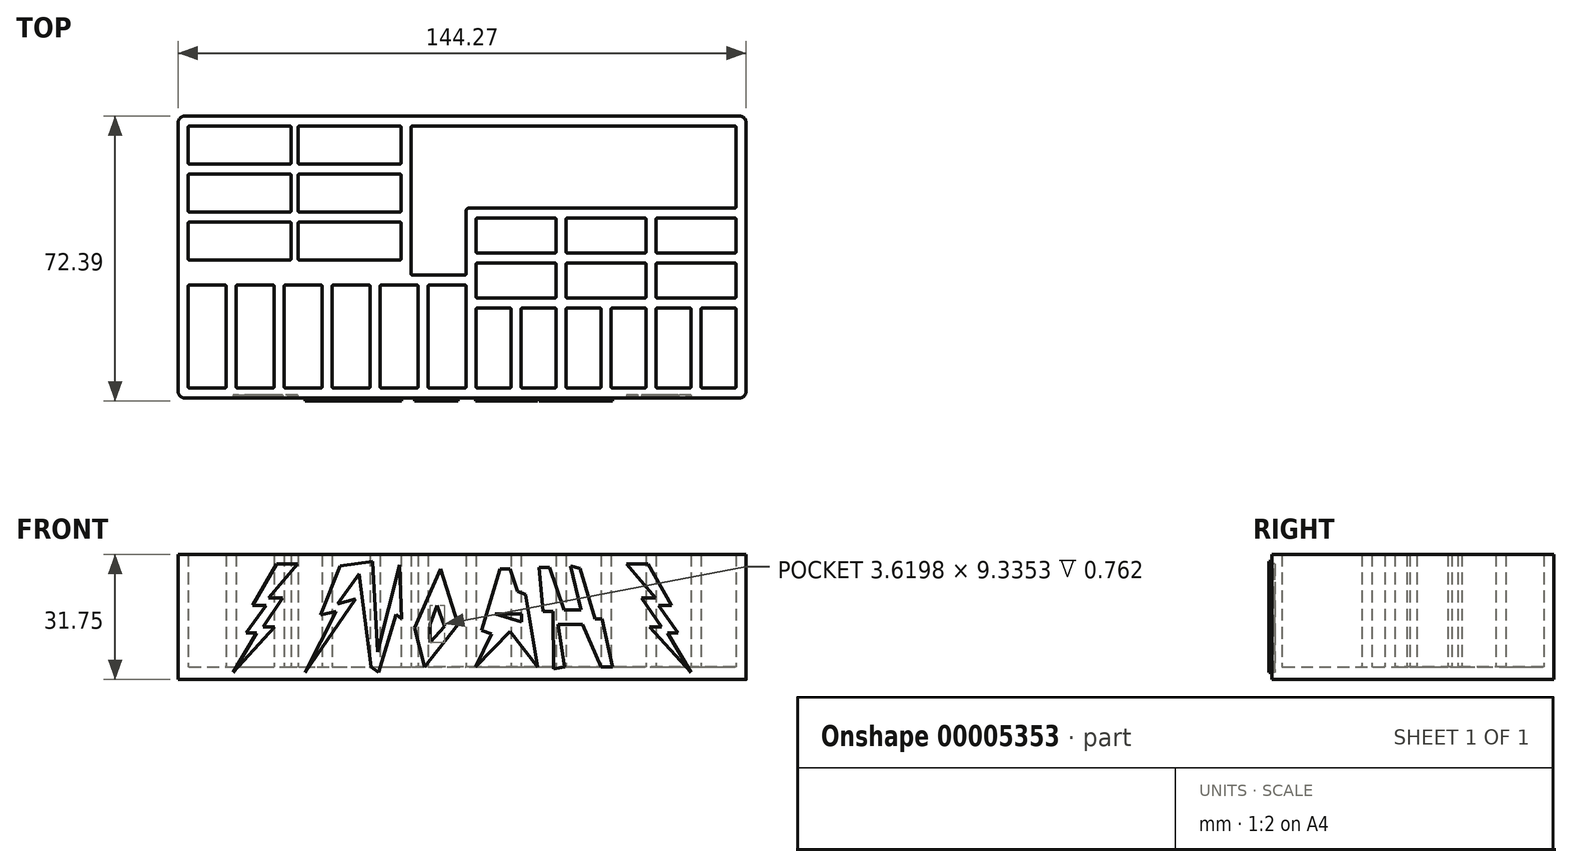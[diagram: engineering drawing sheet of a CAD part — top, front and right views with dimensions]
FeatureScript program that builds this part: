
annotation { "Feature Type Name" : "Feature", "Feature Type Description" : "" }
export const myFeature = defineFeature(function(context is Context, id is Id, definition is map)
    precondition{}
    {
        {
            var Q0;
            Q0=qCreatedBy(makeId("Top.planeOp"),FACE);
            var sketch = newSketch(context, id + "F0", { "sketchPlane" : qUnion([Q0])});
            skLineSegment(sketch, "E0.bottom", {"start": v(0.25, 0) * mm, "end": v(9.4, 0) * mm});
            skLineSegment(sketch, "E0.top", {"start": v(0.25, 26.16) * mm, "end": v(9.4, 26.16) * mm});
            skLineSegment(sketch, "E0.left", {"start": v(0, 0.25) * mm, "end": v(0, 25.9) * mm});
            skLineSegment(sketch, "E0.right", {"start": v(9.65, 0.25) * mm, "end": v(9.65, 25.9) * mm});
            skPoint(sketch, "E1.visualSharp", {"position": v(0, 26.16) * mm});
            skArc(sketch, "E1.filletArc", {"start": v(0.25, 26.16) * mm, "mid": v(0.07, 26.09) * mm, "end": v(0, 25.9) * mm});
            skPoint(sketch, "E2.visualSharp", {"position": v(9.65, 26.16) * mm});
            skArc(sketch, "E2.filletArc", {"start": v(9.65, 25.9) * mm, "mid": v(9.58, 26.09) * mm, "end": v(9.4, 26.16) * mm});
            skPoint(sketch, "E3.visualSharp", {"position": v(9.65, 0) * mm});
            skArc(sketch, "E3.filletArc", {"start": v(9.4, 0) * mm, "mid": v(9.58, 0.07) * mm, "end": v(9.65, 0.25) * mm});
            skPoint(sketch, "E4.visualSharp", {"position": v(0, 0) * mm});
            skArc(sketch, "E4.filletArc", {"start": v(0, 0.25) * mm, "mid": v(0.07, 0.07) * mm, "end": v(0.25, 0) * mm});
            skPoint(sketch, "E5.1.0.0", {"position": v(12.2, 0) * mm});
            skPoint(sketch, "E5.1.0.1", {"position": v(12.2, 26.16) * mm});
            skPoint(sketch, "E5.1.0.2", {"position": v(21.84, 26.16) * mm});
            skLineSegment(sketch, "E5.1.0.3", {"start": v(12.45, 0) * mm, "end": v(21.59, 0) * mm});
            skArc(sketch, "E5.1.0.4", {"start": v(12.2, 0.25) * mm, "mid": v(12.27, 0.07) * mm, "end": v(12.45, 0) * mm});
            skLineSegment(sketch, "E5.1.0.5", {"start": v(12.2, 0.25) * mm, "end": v(12.2, 25.9) * mm});
            skLineSegment(sketch, "E5.1.0.6", {"start": v(12.45, 26.16) * mm, "end": v(21.59, 26.16) * mm});
            skPoint(sketch, "E5.1.0.7", {"position": v(21.84, 0) * mm});
            skArc(sketch, "E5.1.0.8", {"start": v(21.84, 25.9) * mm, "mid": v(21.77, 26.09) * mm, "end": v(21.59, 26.16) * mm});
            skArc(sketch, "E5.1.0.9", {"start": v(21.59, 0) * mm, "mid": v(21.77, 0.07) * mm, "end": v(21.84, 0.25) * mm});
            skLineSegment(sketch, "E5.1.0.10", {"start": v(21.84, 0.25) * mm, "end": v(21.84, 25.9) * mm});
            skArc(sketch, "E5.1.0.11", {"start": v(12.45, 26.16) * mm, "mid": v(12.27, 26.09) * mm, "end": v(12.2, 25.9) * mm});
            skPoint(sketch, "E5.2.0.0", {"position": v(24.38, 0) * mm});
            skPoint(sketch, "E5.2.0.1", {"position": v(24.38, 26.16) * mm});
            skPoint(sketch, "E5.2.0.2", {"position": v(34.04, 26.16) * mm});
            skLineSegment(sketch, "E5.2.0.3", {"start": v(24.64, 0) * mm, "end": v(33.78, 0) * mm});
            skArc(sketch, "E5.2.0.4", {"start": v(24.38, 0.25) * mm, "mid": v(24.46, 0.07) * mm, "end": v(24.64, 0) * mm});
            skLineSegment(sketch, "E5.2.0.5", {"start": v(24.38, 0.25) * mm, "end": v(24.38, 25.9) * mm});
            skLineSegment(sketch, "E5.2.0.6", {"start": v(24.64, 26.16) * mm, "end": v(33.78, 26.16) * mm});
            skPoint(sketch, "E5.2.0.7", {"position": v(34.04, 0) * mm});
            skArc(sketch, "E5.2.0.8", {"start": v(34.04, 25.9) * mm, "mid": v(33.96, 26.09) * mm, "end": v(33.78, 26.16) * mm});
            skArc(sketch, "E5.2.0.9", {"start": v(33.78, 0) * mm, "mid": v(33.96, 0.07) * mm, "end": v(34.04, 0.25) * mm});
            skLineSegment(sketch, "E5.2.0.10", {"start": v(34.04, 0.25) * mm, "end": v(34.04, 25.9) * mm});
            skArc(sketch, "E5.2.0.11", {"start": v(24.64, 26.16) * mm, "mid": v(24.46, 26.09) * mm, "end": v(24.38, 25.9) * mm});
            skPoint(sketch, "E5.3.0.0", {"position": v(36.58, 0) * mm});
            skPoint(sketch, "E5.3.0.1", {"position": v(36.58, 26.16) * mm});
            skPoint(sketch, "E5.3.0.2", {"position": v(46.23, 26.16) * mm});
            skLineSegment(sketch, "E5.3.0.3", {"start": v(36.83, 0) * mm, "end": v(45.97, 0) * mm});
            skArc(sketch, "E5.3.0.4", {"start": v(36.58, 0.25) * mm, "mid": v(36.65, 0.07) * mm, "end": v(36.83, 0) * mm});
            skLineSegment(sketch, "E5.3.0.5", {"start": v(36.58, 0.25) * mm, "end": v(36.58, 25.9) * mm});
            skLineSegment(sketch, "E5.3.0.6", {"start": v(36.83, 26.16) * mm, "end": v(45.97, 26.16) * mm});
            skPoint(sketch, "E5.3.0.7", {"position": v(46.23, 0) * mm});
            skArc(sketch, "E5.3.0.8", {"start": v(46.23, 25.9) * mm, "mid": v(46.15, 26.09) * mm, "end": v(45.97, 26.16) * mm});
            skArc(sketch, "E5.3.0.9", {"start": v(45.97, 0) * mm, "mid": v(46.15, 0.07) * mm, "end": v(46.23, 0.25) * mm});
            skLineSegment(sketch, "E5.3.0.10", {"start": v(46.23, 0.25) * mm, "end": v(46.23, 25.9) * mm});
            skArc(sketch, "E5.3.0.11", {"start": v(36.83, 26.16) * mm, "mid": v(36.65, 26.09) * mm, "end": v(36.58, 25.9) * mm});
            skPoint(sketch, "E5.4.0.0", {"position": v(48.77, 0) * mm});
            skPoint(sketch, "E5.4.0.1", {"position": v(48.77, 26.16) * mm});
            skPoint(sketch, "E5.4.0.2", {"position": v(58.42, 26.16) * mm});
            skLineSegment(sketch, "E5.4.0.3", {"start": v(49.02, 0) * mm, "end": v(58.17, 0) * mm});
            skArc(sketch, "E5.4.0.4", {"start": v(48.77, 0.25) * mm, "mid": v(48.84, 0.07) * mm, "end": v(49.02, 0) * mm});
            skLineSegment(sketch, "E5.4.0.5", {"start": v(48.77, 0.25) * mm, "end": v(48.77, 25.9) * mm});
            skLineSegment(sketch, "E5.4.0.6", {"start": v(49.02, 26.16) * mm, "end": v(58.17, 26.16) * mm});
            skPoint(sketch, "E5.4.0.7", {"position": v(58.42, 0) * mm});
            skArc(sketch, "E5.4.0.8", {"start": v(58.42, 25.9) * mm, "mid": v(58.35, 26.09) * mm, "end": v(58.17, 26.16) * mm});
            skArc(sketch, "E5.4.0.9", {"start": v(58.17, 0) * mm, "mid": v(58.35, 0.07) * mm, "end": v(58.42, 0.25) * mm});
            skLineSegment(sketch, "E5.4.0.10", {"start": v(58.42, 0.25) * mm, "end": v(58.42, 25.9) * mm});
            skArc(sketch, "E5.4.0.11", {"start": v(49.02, 26.16) * mm, "mid": v(48.84, 26.09) * mm, "end": v(48.77, 25.9) * mm});
            skPoint(sketch, "E5.5.0.0", {"position": v(60.96, 0) * mm});
            skPoint(sketch, "E5.5.0.1", {"position": v(60.96, 26.16) * mm});
            skPoint(sketch, "E5.5.0.2", {"position": v(70.61, 26.16) * mm});
            skLineSegment(sketch, "E5.5.0.3", {"start": v(61.21, 0) * mm, "end": v(70.36, 0) * mm});
            skArc(sketch, "E5.5.0.4", {"start": v(60.96, 0.25) * mm, "mid": v(61.03, 0.07) * mm, "end": v(61.21, 0) * mm});
            skLineSegment(sketch, "E5.5.0.5", {"start": v(60.96, 0.25) * mm, "end": v(60.96, 25.9) * mm});
            skLineSegment(sketch, "E5.5.0.6", {"start": v(61.21, 26.16) * mm, "end": v(70.36, 26.16) * mm});
            skPoint(sketch, "E5.5.0.7", {"position": v(70.61, 0) * mm});
            skArc(sketch, "E5.5.0.8", {"start": v(70.61, 25.9) * mm, "mid": v(70.54, 26.09) * mm, "end": v(70.36, 26.16) * mm});
            skArc(sketch, "E5.5.0.9", {"start": v(70.36, 0) * mm, "mid": v(70.54, 0.07) * mm, "end": v(70.61, 0.25) * mm});
            skLineSegment(sketch, "E5.5.0.10", {"start": v(70.61, 0.25) * mm, "end": v(70.61, 25.9) * mm});
            skArc(sketch, "E5.5.0.11", {"start": v(61.21, 26.16) * mm, "mid": v(61.03, 26.09) * mm, "end": v(60.96, 25.9) * mm});
            skLineSegment(sketch, "E5.direction1", {"start": v(0, 0) * mm, "end": v(12.2, 0) * mm, "construction": true});
            skLineSegment(sketch, "E6.bottom", {"start": v(73.4, 0) * mm, "end": v(81.79, 0) * mm});
            skLineSegment(sketch, "E6.top", {"start": v(73.4, 20.32) * mm, "end": v(81.79, 20.32) * mm});
            skLineSegment(sketch, "E6.left", {"start": v(73.15, 0.25) * mm, "end": v(73.15, 20.07) * mm});
            skLineSegment(sketch, "E6.right", {"start": v(82.04, 0.25) * mm, "end": v(82.04, 20.07) * mm});
            skPoint(sketch, "E7.visualSharp", {"position": v(73.15, 20.32) * mm});
            skArc(sketch, "E7.filletArc", {"start": v(73.4, 20.32) * mm, "mid": v(73.23, 20.25) * mm, "end": v(73.15, 20.07) * mm});
            skPoint(sketch, "E8.visualSharp", {"position": v(82.04, 20.32) * mm});
            skArc(sketch, "E8.filletArc", {"start": v(82.04, 20.07) * mm, "mid": v(81.97, 20.25) * mm, "end": v(81.79, 20.32) * mm});
            skPoint(sketch, "E9.visualSharp", {"position": v(82.04, 0) * mm});
            skArc(sketch, "E9.filletArc", {"start": v(81.79, 0) * mm, "mid": v(81.97, 0.07) * mm, "end": v(82.04, 0.25) * mm});
            skPoint(sketch, "E10.visualSharp", {"position": v(73.15, 0) * mm});
            skArc(sketch, "E10.filletArc", {"start": v(73.15, 0.25) * mm, "mid": v(73.23, 0.07) * mm, "end": v(73.4, 0) * mm});
            skLineSegment(sketch, "E11.bottom", {"start": v(0.25, 32.51) * mm, "end": v(25.9, 32.51) * mm});
            skLineSegment(sketch, "E11.top", {"start": v(0.25, 42.16) * mm, "end": v(25.9, 42.16) * mm});
            skLineSegment(sketch, "E11.left", {"start": v(0, 32.77) * mm, "end": v(0, 41.91) * mm});
            skLineSegment(sketch, "E11.right", {"start": v(26.16, 32.77) * mm, "end": v(26.16, 41.91) * mm});
            skPoint(sketch, "E12.visualSharp", {"position": v(0, 42.16) * mm});
            skArc(sketch, "E12.filletArc", {"start": v(0.25, 42.16) * mm, "mid": v(0.07, 42.09) * mm, "end": v(0, 41.91) * mm});
            skPoint(sketch, "E13.visualSharp", {"position": v(26.16, 42.16) * mm});
            skArc(sketch, "E13.filletArc", {"start": v(26.16, 41.91) * mm, "mid": v(26.09, 42.09) * mm, "end": v(25.9, 42.16) * mm});
            skPoint(sketch, "E14.visualSharp", {"position": v(26.16, 32.51) * mm});
            skArc(sketch, "E14.filletArc", {"start": v(25.9, 32.51) * mm, "mid": v(26.09, 32.59) * mm, "end": v(26.16, 32.77) * mm});
            skPoint(sketch, "E15.visualSharp", {"position": v(0, 32.51) * mm});
            skArc(sketch, "E15.filletArc", {"start": v(0, 32.77) * mm, "mid": v(0.07, 32.59) * mm, "end": v(0.25, 32.51) * mm});
            skLineSegment(sketch, "E16.0.1.0", {"start": v(0, 44.96) * mm, "end": v(0, 54.1) * mm});
            skPoint(sketch, "E16.0.1.1", {"position": v(0, 54.36) * mm});
            skArc(sketch, "E16.0.1.2", {"start": v(0.25, 54.36) * mm, "mid": v(0.07, 54.28) * mm, "end": v(0, 54.1) * mm});
            skLineSegment(sketch, "E16.0.1.3", {"start": v(0.25, 54.36) * mm, "end": v(25.9, 54.36) * mm});
            skPoint(sketch, "E16.0.1.4", {"position": v(26.16, 44.7) * mm});
            skPoint(sketch, "E16.0.1.5", {"position": v(26.16, 54.36) * mm});
            skLineSegment(sketch, "E16.0.1.6", {"start": v(0.25, 44.7) * mm, "end": v(25.9, 44.7) * mm});
            skPoint(sketch, "E16.0.1.7", {"position": v(0, 44.7) * mm});
            skLineSegment(sketch, "E16.0.1.8", {"start": v(26.16, 44.96) * mm, "end": v(26.16, 54.1) * mm});
            skArc(sketch, "E16.0.1.9", {"start": v(26.16, 54.1) * mm, "mid": v(26.09, 54.28) * mm, "end": v(25.9, 54.36) * mm});
            skArc(sketch, "E16.0.1.10", {"start": v(25.9, 44.7) * mm, "mid": v(26.09, 44.78) * mm, "end": v(26.16, 44.96) * mm});
            skArc(sketch, "E16.0.1.11", {"start": v(0, 44.96) * mm, "mid": v(0.07, 44.78) * mm, "end": v(0.25, 44.7) * mm});
            skLineSegment(sketch, "E16.1.0.0", {"start": v(27.94, 32.77) * mm, "end": v(27.94, 41.91) * mm});
            skPoint(sketch, "E16.1.0.1", {"position": v(27.94, 42.16) * mm});
            skArc(sketch, "E16.1.0.2", {"start": v(28.2, 42.16) * mm, "mid": v(28.01, 42.09) * mm, "end": v(27.94, 41.91) * mm});
            skLineSegment(sketch, "E16.1.0.3", {"start": v(28.2, 42.16) * mm, "end": v(53.85, 42.16) * mm});
            skPoint(sketch, "E16.1.0.4", {"position": v(54.1, 32.51) * mm});
            skPoint(sketch, "E16.1.0.5", {"position": v(54.1, 42.16) * mm});
            skLineSegment(sketch, "E16.1.0.6", {"start": v(28.2, 32.51) * mm, "end": v(53.85, 32.51) * mm});
            skPoint(sketch, "E16.1.0.7", {"position": v(27.94, 32.51) * mm});
            skLineSegment(sketch, "E16.1.0.8", {"start": v(54.1, 32.77) * mm, "end": v(54.1, 41.91) * mm});
            skArc(sketch, "E16.1.0.9", {"start": v(54.1, 41.91) * mm, "mid": v(54.03, 42.09) * mm, "end": v(53.85, 42.16) * mm});
            skArc(sketch, "E16.1.0.10", {"start": v(53.85, 32.51) * mm, "mid": v(54.03, 32.59) * mm, "end": v(54.1, 32.77) * mm});
            skArc(sketch, "E16.1.0.11", {"start": v(27.94, 32.77) * mm, "mid": v(28.01, 32.59) * mm, "end": v(28.2, 32.51) * mm});
            skLineSegment(sketch, "E16.1.1.0", {"start": v(27.94, 44.96) * mm, "end": v(27.94, 54.1) * mm});
            skPoint(sketch, "E16.1.1.1", {"position": v(27.94, 54.36) * mm});
            skArc(sketch, "E16.1.1.2", {"start": v(28.2, 54.36) * mm, "mid": v(28.01, 54.28) * mm, "end": v(27.94, 54.1) * mm});
            skLineSegment(sketch, "E16.1.1.3", {"start": v(28.2, 54.36) * mm, "end": v(53.85, 54.36) * mm});
            skPoint(sketch, "E16.1.1.4", {"position": v(54.1, 44.7) * mm});
            skPoint(sketch, "E16.1.1.5", {"position": v(54.1, 54.36) * mm});
            skLineSegment(sketch, "E16.1.1.6", {"start": v(28.2, 44.7) * mm, "end": v(53.85, 44.7) * mm});
            skPoint(sketch, "E16.1.1.7", {"position": v(27.94, 44.7) * mm});
            skLineSegment(sketch, "E16.1.1.8", {"start": v(54.1, 44.96) * mm, "end": v(54.1, 54.1) * mm});
            skArc(sketch, "E16.1.1.9", {"start": v(54.1, 54.1) * mm, "mid": v(54.03, 54.28) * mm, "end": v(53.85, 54.36) * mm});
            skArc(sketch, "E16.1.1.10", {"start": v(53.85, 44.7) * mm, "mid": v(54.03, 44.78) * mm, "end": v(54.1, 44.96) * mm});
            skArc(sketch, "E16.1.1.11", {"start": v(27.94, 44.96) * mm, "mid": v(28.01, 44.78) * mm, "end": v(28.2, 44.7) * mm});
            skLineSegment(sketch, "E16.direction1", {"start": v(0, 32.77) * mm, "end": v(27.94, 32.77) * mm, "construction": true});
            skLineSegment(sketch, "E16.direction2", {"start": v(0, 32.77) * mm, "end": v(0, 44.96) * mm, "construction": true});
            skPoint(sketch, "E17.1.0.0", {"position": v(84.58, 0) * mm});
            skLineSegment(sketch, "E17.1.0.1", {"start": v(93.47, 0.25) * mm, "end": v(93.47, 20.07) * mm});
            skLineSegment(sketch, "E17.1.0.2", {"start": v(84.58, 0.25) * mm, "end": v(84.58, 20.07) * mm});
            skPoint(sketch, "E17.1.0.3", {"position": v(84.58, 20.32) * mm});
            skArc(sketch, "E17.1.0.4", {"start": v(84.84, 20.32) * mm, "mid": v(84.66, 20.25) * mm, "end": v(84.58, 20.07) * mm});
            skPoint(sketch, "E17.1.0.5", {"position": v(93.47, 20.32) * mm});
            skPoint(sketch, "E17.1.0.6", {"position": v(93.47, 0) * mm});
            skLineSegment(sketch, "E17.1.0.7", {"start": v(84.84, 20.32) * mm, "end": v(93.22, 20.32) * mm});
            skLineSegment(sketch, "E17.1.0.8", {"start": v(84.84, 0) * mm, "end": v(93.22, 0) * mm});
            skArc(sketch, "E17.1.0.9", {"start": v(93.47, 20.07) * mm, "mid": v(93.4, 20.25) * mm, "end": v(93.22, 20.32) * mm});
            skArc(sketch, "E17.1.0.10", {"start": v(93.22, 0) * mm, "mid": v(93.4, 0.07) * mm, "end": v(93.47, 0.25) * mm});
            skArc(sketch, "E17.1.0.11", {"start": v(84.58, 0.25) * mm, "mid": v(84.66, 0.07) * mm, "end": v(84.84, 0) * mm});
            skPoint(sketch, "E17.2.0.0", {"position": v(96.01, 0) * mm});
            skLineSegment(sketch, "E17.2.0.1", {"start": v(104.9, 0.25) * mm, "end": v(104.9, 20.07) * mm});
            skLineSegment(sketch, "E17.2.0.2", {"start": v(96.01, 0.25) * mm, "end": v(96.01, 20.07) * mm});
            skPoint(sketch, "E17.2.0.3", {"position": v(96.01, 20.32) * mm});
            skArc(sketch, "E17.2.0.4", {"start": v(96.27, 20.32) * mm, "mid": v(96.09, 20.25) * mm, "end": v(96.01, 20.07) * mm});
            skPoint(sketch, "E17.2.0.5", {"position": v(104.9, 20.32) * mm});
            skPoint(sketch, "E17.2.0.6", {"position": v(104.9, 0) * mm});
            skLineSegment(sketch, "E17.2.0.7", {"start": v(96.27, 20.32) * mm, "end": v(104.65, 20.32) * mm});
            skLineSegment(sketch, "E17.2.0.8", {"start": v(96.27, 0) * mm, "end": v(104.65, 0) * mm});
            skArc(sketch, "E17.2.0.9", {"start": v(104.9, 20.07) * mm, "mid": v(104.83, 20.25) * mm, "end": v(104.65, 20.32) * mm});
            skArc(sketch, "E17.2.0.10", {"start": v(104.65, 0) * mm, "mid": v(104.83, 0.07) * mm, "end": v(104.9, 0.25) * mm});
            skArc(sketch, "E17.2.0.11", {"start": v(96.01, 0.25) * mm, "mid": v(96.09, 0.07) * mm, "end": v(96.27, 0) * mm});
            skPoint(sketch, "E17.3.0.0", {"position": v(107.44, 0) * mm});
            skLineSegment(sketch, "E17.3.0.1", {"start": v(116.33, 0.25) * mm, "end": v(116.33, 20.07) * mm});
            skLineSegment(sketch, "E17.3.0.2", {"start": v(107.44, 0.25) * mm, "end": v(107.44, 20.07) * mm});
            skPoint(sketch, "E17.3.0.3", {"position": v(107.44, 20.32) * mm});
            skArc(sketch, "E17.3.0.4", {"start": v(107.7, 20.32) * mm, "mid": v(107.52, 20.25) * mm, "end": v(107.44, 20.07) * mm});
            skPoint(sketch, "E17.3.0.5", {"position": v(116.33, 20.32) * mm});
            skPoint(sketch, "E17.3.0.6", {"position": v(116.33, 0) * mm});
            skLineSegment(sketch, "E17.3.0.7", {"start": v(107.7, 20.32) * mm, "end": v(116.08, 20.32) * mm});
            skLineSegment(sketch, "E17.3.0.8", {"start": v(107.7, 0) * mm, "end": v(116.08, 0) * mm});
            skArc(sketch, "E17.3.0.9", {"start": v(116.33, 20.07) * mm, "mid": v(116.26, 20.25) * mm, "end": v(116.08, 20.32) * mm});
            skArc(sketch, "E17.3.0.10", {"start": v(116.08, 0) * mm, "mid": v(116.26, 0.07) * mm, "end": v(116.33, 0.25) * mm});
            skArc(sketch, "E17.3.0.11", {"start": v(107.44, 0.25) * mm, "mid": v(107.52, 0.07) * mm, "end": v(107.7, 0) * mm});
            skPoint(sketch, "E17.4.0.0", {"position": v(118.87, 0) * mm});
            skLineSegment(sketch, "E17.4.0.1", {"start": v(127.76, 0.25) * mm, "end": v(127.76, 20.07) * mm});
            skLineSegment(sketch, "E17.4.0.2", {"start": v(118.87, 0.25) * mm, "end": v(118.87, 20.07) * mm});
            skPoint(sketch, "E17.4.0.3", {"position": v(118.87, 20.32) * mm});
            skArc(sketch, "E17.4.0.4", {"start": v(119.13, 20.32) * mm, "mid": v(118.95, 20.25) * mm, "end": v(118.87, 20.07) * mm});
            skPoint(sketch, "E17.4.0.5", {"position": v(127.76, 20.32) * mm});
            skPoint(sketch, "E17.4.0.6", {"position": v(127.76, 0) * mm});
            skLineSegment(sketch, "E17.4.0.7", {"start": v(119.13, 20.32) * mm, "end": v(127.5, 20.32) * mm});
            skLineSegment(sketch, "E17.4.0.8", {"start": v(119.13, 0) * mm, "end": v(127.5, 0) * mm});
            skArc(sketch, "E17.4.0.9", {"start": v(127.76, 20.07) * mm, "mid": v(127.69, 20.25) * mm, "end": v(127.5, 20.32) * mm});
            skArc(sketch, "E17.4.0.10", {"start": v(127.5, 0) * mm, "mid": v(127.69, 0.07) * mm, "end": v(127.76, 0.25) * mm});
            skArc(sketch, "E17.4.0.11", {"start": v(118.87, 0.25) * mm, "mid": v(118.95, 0.07) * mm, "end": v(119.13, 0) * mm});
            skPoint(sketch, "E17.5.0.0", {"position": v(130.3, 0) * mm});
            skLineSegment(sketch, "E17.5.0.1", {"start": v(139.2, 0.25) * mm, "end": v(139.2, 20.07) * mm});
            skLineSegment(sketch, "E17.5.0.2", {"start": v(130.3, 0.25) * mm, "end": v(130.3, 20.07) * mm});
            skPoint(sketch, "E17.5.0.3", {"position": v(130.3, 20.32) * mm});
            skArc(sketch, "E17.5.0.4", {"start": v(130.56, 20.32) * mm, "mid": v(130.38, 20.25) * mm, "end": v(130.3, 20.07) * mm});
            skPoint(sketch, "E17.5.0.5", {"position": v(139.2, 20.32) * mm});
            skPoint(sketch, "E17.5.0.6", {"position": v(139.2, 0) * mm});
            skLineSegment(sketch, "E17.5.0.7", {"start": v(130.56, 20.32) * mm, "end": v(138.94, 20.32) * mm});
            skLineSegment(sketch, "E17.5.0.8", {"start": v(130.56, 0) * mm, "end": v(138.94, 0) * mm});
            skArc(sketch, "E17.5.0.9", {"start": v(139.2, 20.07) * mm, "mid": v(139.12, 20.25) * mm, "end": v(138.94, 20.32) * mm});
            skArc(sketch, "E17.5.0.10", {"start": v(138.94, 0) * mm, "mid": v(139.12, 0.07) * mm, "end": v(139.2, 0.25) * mm});
            skArc(sketch, "E17.5.0.11", {"start": v(130.3, 0.25) * mm, "mid": v(130.38, 0.07) * mm, "end": v(130.56, 0) * mm});
            skLineSegment(sketch, "E17.direction1", {"start": v(73.15, 0) * mm, "end": v(84.58, 0) * mm, "construction": true});
            skLineSegment(sketch, "E18.bottom", {"start": v(73.4, 22.86) * mm, "end": v(93.22, 22.86) * mm});
            skLineSegment(sketch, "E18.top", {"start": v(73.4, 31.75) * mm, "end": v(93.22, 31.75) * mm});
            skLineSegment(sketch, "E18.left", {"start": v(73.15, 23.11) * mm, "end": v(73.15, 31.5) * mm});
            skLineSegment(sketch, "E18.right", {"start": v(93.47, 23.11) * mm, "end": v(93.47, 31.5) * mm});
            skPoint(sketch, "E19.visualSharp", {"position": v(73.15, 31.75) * mm});
            skArc(sketch, "E19.filletArc", {"start": v(73.4, 31.75) * mm, "mid": v(73.23, 31.68) * mm, "end": v(73.15, 31.5) * mm});
            skPoint(sketch, "E20.visualSharp", {"position": v(73.15, 22.86) * mm});
            skArc(sketch, "E20.filletArc", {"start": v(73.15, 23.11) * mm, "mid": v(73.23, 22.93) * mm, "end": v(73.4, 22.86) * mm});
            skPoint(sketch, "E21.visualSharp", {"position": v(93.47, 22.86) * mm});
            skArc(sketch, "E21.filletArc", {"start": v(93.22, 22.86) * mm, "mid": v(93.4, 22.93) * mm, "end": v(93.47, 23.11) * mm});
            skPoint(sketch, "E22.visualSharp", {"position": v(93.47, 31.75) * mm});
            skArc(sketch, "E22.filletArc", {"start": v(93.47, 31.5) * mm, "mid": v(93.4, 31.68) * mm, "end": v(93.22, 31.75) * mm});
            skLineSegment(sketch, "E23.0.0.2", {"start": v(0, 57.15) * mm, "end": v(0, 66.3) * mm});
            skPoint(sketch, "E23.3.0.2", {"position": v(0, 66.55) * mm});
            skArc(sketch, "E23.4.0.2", {"start": v(0.25, 66.55) * mm, "mid": v(0.07, 66.47) * mm, "end": v(0, 66.3) * mm});
            skLineSegment(sketch, "E23.8.0.2", {"start": v(0.25, 66.55) * mm, "end": v(25.9, 66.55) * mm});
            skPoint(sketch, "E23.11.0.2", {"position": v(26.16, 56.9) * mm});
            skPoint(sketch, "E23.12.0.2", {"position": v(26.16, 66.55) * mm});
            skLineSegment(sketch, "E23.13.0.2", {"start": v(0.25, 56.9) * mm, "end": v(25.9, 56.9) * mm});
            skPoint(sketch, "E23.16.0.2", {"position": v(0, 56.9) * mm});
            skLineSegment(sketch, "E23.17.0.2", {"start": v(26.16, 57.15) * mm, "end": v(26.16, 66.3) * mm});
            skArc(sketch, "E23.20.0.2", {"start": v(26.16, 66.3) * mm, "mid": v(26.09, 66.47) * mm, "end": v(25.9, 66.55) * mm});
            skArc(sketch, "E23.24.0.2", {"start": v(25.9, 56.9) * mm, "mid": v(26.09, 56.97) * mm, "end": v(26.16, 57.15) * mm});
            skArc(sketch, "E23.28.0.2", {"start": v(0, 57.15) * mm, "mid": v(0.07, 56.97) * mm, "end": v(0.25, 56.9) * mm});
            skLineSegment(sketch, "E23.0.1.2", {"start": v(27.94, 57.15) * mm, "end": v(27.94, 66.3) * mm});
            skPoint(sketch, "E23.3.1.2", {"position": v(27.94, 66.55) * mm});
            skArc(sketch, "E23.4.1.2", {"start": v(28.2, 66.55) * mm, "mid": v(28.01, 66.47) * mm, "end": v(27.94, 66.3) * mm});
            skLineSegment(sketch, "E23.8.1.2", {"start": v(28.2, 66.55) * mm, "end": v(53.85, 66.55) * mm});
            skPoint(sketch, "E23.11.1.2", {"position": v(54.1, 56.9) * mm});
            skPoint(sketch, "E23.12.1.2", {"position": v(54.1, 66.55) * mm});
            skLineSegment(sketch, "E23.13.1.2", {"start": v(28.2, 56.9) * mm, "end": v(53.85, 56.9) * mm});
            skPoint(sketch, "E23.16.1.2", {"position": v(27.94, 56.9) * mm});
            skLineSegment(sketch, "E23.17.1.2", {"start": v(54.1, 57.15) * mm, "end": v(54.1, 66.3) * mm});
            skArc(sketch, "E23.20.1.2", {"start": v(54.1, 66.3) * mm, "mid": v(54.03, 66.47) * mm, "end": v(53.85, 66.55) * mm});
            skArc(sketch, "E23.24.1.2", {"start": v(53.85, 56.9) * mm, "mid": v(54.03, 56.97) * mm, "end": v(54.1, 57.15) * mm});
            skArc(sketch, "E23.28.1.2", {"start": v(27.94, 57.15) * mm, "mid": v(28.01, 56.97) * mm, "end": v(28.2, 56.9) * mm});
            skLineSegment(sketch, "E24.0.1.0", {"start": v(73.15, 34.54) * mm, "end": v(73.15, 42.93) * mm});
            skLineSegment(sketch, "E24.0.1.1", {"start": v(73.4, 43.18) * mm, "end": v(93.22, 43.18) * mm});
            skPoint(sketch, "E24.0.1.2", {"position": v(93.47, 43.18) * mm});
            skArc(sketch, "E24.0.1.3", {"start": v(93.22, 34.29) * mm, "mid": v(93.4, 34.36) * mm, "end": v(93.47, 34.54) * mm});
            skPoint(sketch, "E24.0.1.4", {"position": v(93.47, 34.3) * mm});
            skArc(sketch, "E24.0.1.5", {"start": v(73.15, 34.54) * mm, "mid": v(73.23, 34.36) * mm, "end": v(73.4, 34.3) * mm});
            skLineSegment(sketch, "E24.0.1.6", {"start": v(93.47, 34.54) * mm, "end": v(93.47, 42.93) * mm});
            skLineSegment(sketch, "E24.0.1.7", {"start": v(73.4, 34.3) * mm, "end": v(93.22, 34.3) * mm});
            skPoint(sketch, "E24.0.1.8", {"position": v(73.15, 43.18) * mm});
            skPoint(sketch, "E24.0.1.9", {"position": v(73.15, 34.3) * mm});
            skArc(sketch, "E24.0.1.10", {"start": v(93.47, 42.93) * mm, "mid": v(93.4, 43.1) * mm, "end": v(93.22, 43.18) * mm});
            skArc(sketch, "E24.0.1.11", {"start": v(73.4, 43.18) * mm, "mid": v(73.23, 43.1) * mm, "end": v(73.15, 42.93) * mm});
            skLineSegment(sketch, "E24.1.0.0", {"start": v(96.01, 23.11) * mm, "end": v(96.01, 31.5) * mm});
            skLineSegment(sketch, "E24.1.0.1", {"start": v(96.27, 31.75) * mm, "end": v(116.08, 31.75) * mm});
            skPoint(sketch, "E24.1.0.2", {"position": v(116.33, 31.75) * mm});
            skArc(sketch, "E24.1.0.3", {"start": v(116.08, 22.86) * mm, "mid": v(116.26, 22.93) * mm, "end": v(116.33, 23.11) * mm});
            skPoint(sketch, "E24.1.0.4", {"position": v(116.33, 22.86) * mm});
            skArc(sketch, "E24.1.0.5", {"start": v(96.01, 23.11) * mm, "mid": v(96.09, 22.93) * mm, "end": v(96.27, 22.86) * mm});
            skLineSegment(sketch, "E24.1.0.6", {"start": v(116.33, 23.11) * mm, "end": v(116.33, 31.5) * mm});
            skLineSegment(sketch, "E24.1.0.7", {"start": v(96.27, 22.86) * mm, "end": v(116.08, 22.86) * mm});
            skPoint(sketch, "E24.1.0.8", {"position": v(96.01, 31.75) * mm});
            skPoint(sketch, "E24.1.0.9", {"position": v(96.01, 22.86) * mm});
            skArc(sketch, "E24.1.0.10", {"start": v(116.33, 31.5) * mm, "mid": v(116.26, 31.68) * mm, "end": v(116.08, 31.75) * mm});
            skArc(sketch, "E24.1.0.11", {"start": v(96.27, 31.75) * mm, "mid": v(96.09, 31.68) * mm, "end": v(96.01, 31.5) * mm});
            skLineSegment(sketch, "E24.1.1.0", {"start": v(96.01, 34.54) * mm, "end": v(96.01, 42.93) * mm});
            skLineSegment(sketch, "E24.1.1.1", {"start": v(96.27, 43.18) * mm, "end": v(116.08, 43.18) * mm});
            skPoint(sketch, "E24.1.1.2", {"position": v(116.33, 43.18) * mm});
            skArc(sketch, "E24.1.1.3", {"start": v(116.08, 34.29) * mm, "mid": v(116.26, 34.36) * mm, "end": v(116.33, 34.54) * mm});
            skPoint(sketch, "E24.1.1.4", {"position": v(116.33, 34.3) * mm});
            skArc(sketch, "E24.1.1.5", {"start": v(96.01, 34.54) * mm, "mid": v(96.09, 34.36) * mm, "end": v(96.27, 34.3) * mm});
            skLineSegment(sketch, "E24.1.1.6", {"start": v(116.33, 34.54) * mm, "end": v(116.33, 42.93) * mm});
            skLineSegment(sketch, "E24.1.1.7", {"start": v(96.27, 34.3) * mm, "end": v(116.08, 34.3) * mm});
            skPoint(sketch, "E24.1.1.8", {"position": v(96.01, 43.18) * mm});
            skPoint(sketch, "E24.1.1.9", {"position": v(96.01, 34.3) * mm});
            skArc(sketch, "E24.1.1.10", {"start": v(116.33, 42.93) * mm, "mid": v(116.26, 43.1) * mm, "end": v(116.08, 43.18) * mm});
            skArc(sketch, "E24.1.1.11", {"start": v(96.27, 43.18) * mm, "mid": v(96.09, 43.1) * mm, "end": v(96.01, 42.93) * mm});
            skLineSegment(sketch, "E24.2.0.0", {"start": v(118.87, 23.11) * mm, "end": v(118.87, 31.5) * mm});
            skLineSegment(sketch, "E24.2.0.1", {"start": v(119.13, 31.75) * mm, "end": v(138.94, 31.75) * mm});
            skPoint(sketch, "E24.2.0.2", {"position": v(139.2, 31.75) * mm});
            skArc(sketch, "E24.2.0.3", {"start": v(138.94, 22.86) * mm, "mid": v(139.12, 22.93) * mm, "end": v(139.2, 23.11) * mm});
            skPoint(sketch, "E24.2.0.4", {"position": v(139.2, 22.86) * mm});
            skArc(sketch, "E24.2.0.5", {"start": v(118.87, 23.11) * mm, "mid": v(118.95, 22.93) * mm, "end": v(119.13, 22.86) * mm});
            skLineSegment(sketch, "E24.2.0.6", {"start": v(139.2, 23.11) * mm, "end": v(139.2, 31.5) * mm});
            skLineSegment(sketch, "E24.2.0.7", {"start": v(119.13, 22.86) * mm, "end": v(138.94, 22.86) * mm});
            skPoint(sketch, "E24.2.0.8", {"position": v(118.87, 31.75) * mm});
            skPoint(sketch, "E24.2.0.9", {"position": v(118.87, 22.86) * mm});
            skArc(sketch, "E24.2.0.10", {"start": v(139.2, 31.5) * mm, "mid": v(139.12, 31.68) * mm, "end": v(138.94, 31.75) * mm});
            skArc(sketch, "E24.2.0.11", {"start": v(119.13, 31.75) * mm, "mid": v(118.95, 31.68) * mm, "end": v(118.87, 31.5) * mm});
            skLineSegment(sketch, "E24.2.1.0", {"start": v(118.87, 34.54) * mm, "end": v(118.87, 42.93) * mm});
            skLineSegment(sketch, "E24.2.1.1", {"start": v(119.13, 43.18) * mm, "end": v(138.94, 43.18) * mm});
            skPoint(sketch, "E24.2.1.2", {"position": v(139.2, 43.18) * mm});
            skArc(sketch, "E24.2.1.3", {"start": v(138.94, 34.29) * mm, "mid": v(139.12, 34.36) * mm, "end": v(139.2, 34.54) * mm});
            skPoint(sketch, "E24.2.1.4", {"position": v(139.2, 34.3) * mm});
            skArc(sketch, "E24.2.1.5", {"start": v(118.87, 34.54) * mm, "mid": v(118.95, 34.36) * mm, "end": v(119.13, 34.3) * mm});
            skLineSegment(sketch, "E24.2.1.6", {"start": v(139.2, 34.54) * mm, "end": v(139.2, 42.93) * mm});
            skLineSegment(sketch, "E24.2.1.7", {"start": v(119.13, 34.3) * mm, "end": v(138.94, 34.3) * mm});
            skPoint(sketch, "E24.2.1.8", {"position": v(118.87, 43.18) * mm});
            skPoint(sketch, "E24.2.1.9", {"position": v(118.87, 34.3) * mm});
            skArc(sketch, "E24.2.1.10", {"start": v(139.2, 42.93) * mm, "mid": v(139.12, 43.1) * mm, "end": v(138.94, 43.18) * mm});
            skArc(sketch, "E24.2.1.11", {"start": v(119.13, 43.18) * mm, "mid": v(118.95, 43.1) * mm, "end": v(118.87, 42.93) * mm});
            skLineSegment(sketch, "E24.direction1", {"start": v(73.15, 23.11) * mm, "end": v(96.01, 23.11) * mm, "construction": true});
            skLineSegment(sketch, "E24.direction2", {"start": v(73.15, 23.11) * mm, "end": v(73.15, 34.54) * mm, "construction": true});
            skLineSegment(sketch, "E25", {"start": v(56.9, 28.7) * mm, "end": v(70.36, 28.7) * mm});
            skLineSegment(sketch, "E26", {"start": v(70.61, 28.96) * mm, "end": v(70.61, 44.96) * mm});
            skLineSegment(sketch, "E27", {"start": v(71.37, 45.72) * mm, "end": v(138.94, 45.72) * mm});
            skLineSegment(sketch, "E28", {"start": v(139.2, 45.97) * mm, "end": v(139.2, 66.3) * mm});
            skLineSegment(sketch, "E29", {"start": v(138.94, 66.55) * mm, "end": v(56.9, 66.55) * mm});
            skLineSegment(sketch, "E30", {"start": v(56.64, 66.3) * mm, "end": v(56.64, 28.96) * mm});
            skPoint(sketch, "E31.visualSharp", {"position": v(56.64, 66.55) * mm});
            skArc(sketch, "E31.filletArc", {"start": v(56.9, 66.55) * mm, "mid": v(56.72, 66.47) * mm, "end": v(56.64, 66.3) * mm});
            skPoint(sketch, "E32.visualSharp", {"position": v(139.2, 66.55) * mm});
            skArc(sketch, "E32.filletArc", {"start": v(139.2, 66.3) * mm, "mid": v(139.12, 66.47) * mm, "end": v(138.94, 66.55) * mm});
            skPoint(sketch, "E33.visualSharp", {"position": v(139.2, 45.72) * mm});
            skArc(sketch, "E33.filletArc", {"start": v(138.94, 45.72) * mm, "mid": v(139.12, 45.8) * mm, "end": v(139.2, 45.97) * mm});
            skPoint(sketch, "E34.visualSharp", {"position": v(70.61, 28.7) * mm});
            skArc(sketch, "E34.filletArc", {"start": v(70.36, 28.7) * mm, "mid": v(70.54, 28.78) * mm, "end": v(70.61, 28.96) * mm});
            skPoint(sketch, "E35.visualSharp", {"position": v(56.64, 28.7) * mm});
            skArc(sketch, "E35.filletArc", {"start": v(56.64, 28.96) * mm, "mid": v(56.72, 28.78) * mm, "end": v(56.9, 28.7) * mm});
            skPoint(sketch, "E36.visualSharp", {"position": v(70.61, 45.72) * mm});
            skArc(sketch, "E36.filletArc", {"start": v(71.37, 45.72) * mm, "mid": v(70.84, 45.5) * mm, "end": v(70.61, 44.96) * mm});
            skLineSegment(sketch, "E37.bottom", {"start": v(-0.95, 69.09) * mm, "end": v(140.14, 69.09) * mm});
            skLineSegment(sketch, "E37.top", {"start": v(-0.95, -2.54) * mm, "end": v(140.14, -2.54) * mm});
            skLineSegment(sketch, "E37.left", {"start": v(-2.54, 67.5) * mm, "end": v(-2.54, -0.95) * mm});
            skLineSegment(sketch, "E37.right", {"start": v(141.73, 67.5) * mm, "end": v(141.73, -0.95) * mm});
            skPoint(sketch, "E38.visualSharp", {"position": v(-2.54, 69.09) * mm});
            skArc(sketch, "E38.filletArc", {"start": v(-0.95, 69.09) * mm, "mid": v(-2.08, 68.62) * mm, "end": v(-2.54, 67.5) * mm});
            skPoint(sketch, "E39.visualSharp", {"position": v(141.73, 69.09) * mm});
            skArc(sketch, "E39.filletArc", {"start": v(141.73, 67.5) * mm, "mid": v(141.27, 68.62) * mm, "end": v(140.14, 69.09) * mm});
            skPoint(sketch, "E40.visualSharp", {"position": v(141.73, -2.54) * mm});
            skArc(sketch, "E40.filletArc", {"start": v(140.14, -2.54) * mm, "mid": v(141.27, -2.08) * mm, "end": v(141.73, -0.95) * mm});
            skPoint(sketch, "E41.visualSharp", {"position": v(-2.54, -2.54) * mm});
            skArc(sketch, "E41.filletArc", {"start": v(-2.54, -0.95) * mm, "mid": v(-2.08, -2.08) * mm, "end": v(-0.95, -2.54) * mm});
            skSolve(sketch);
        }
        {
            var Q0;
            Q0 = qSketchRegion(id + "F0", true);
            extrude(context, id + "F1", {"entities" : qUnion([Q0]), "depth" : 28.57 * mm});
        }
        {
            var Q0;
            Q0=makeQuery(id+"F1.opExtrude","CAP_FACE",FACE,{"disambiguationData":[OSD([sQuery(id+"F0.wireOp",EDGE,"E0.bottom"),sQuery(id+"F0.wireOp",EDGE,"E0.top"),sQuery(id+"F0.wireOp",EDGE,"E0.left"),sQuery(id+"F0.wireOp",EDGE,"E0.right"),sQuery(id+"F0.wireOp",EDGE,"E1.filletArc"),sQuery(id+"F0.wireOp",EDGE,"E2.filletArc"),sQuery(id+"F0.wireOp",EDGE,"E3.filletArc"),sQuery(id+"F0.wireOp",EDGE,"E4.filletArc"),sQuery(id+"F0.wireOp",EDGE,"E5.1.0.3"),sQuery(id+"F0.wireOp",EDGE,"E5.1.0.4"),sQuery(id+"F0.wireOp",EDGE,"E5.1.0.5"),sQuery(id+"F0.wireOp",EDGE,"E5.1.0.6"),sQuery(id+"F0.wireOp",EDGE,"E5.1.0.8"),sQuery(id+"F0.wireOp",EDGE,"E5.1.0.9"),sQuery(id+"F0.wireOp",EDGE,"E5.1.0.10"),sQuery(id+"F0.wireOp",EDGE,"E5.1.0.11"),sQuery(id+"F0.wireOp",EDGE,"E5.2.0.3"),sQuery(id+"F0.wireOp",EDGE,"E5.2.0.4"),sQuery(id+"F0.wireOp",EDGE,"E5.2.0.5"),sQuery(id+"F0.wireOp",EDGE,"E5.2.0.6"),sQuery(id+"F0.wireOp",EDGE,"E5.2.0.8"),sQuery(id+"F0.wireOp",EDGE,"E5.2.0.9"),sQuery(id+"F0.wireOp",EDGE,"E5.2.0.10"),sQuery(id+"F0.wireOp",EDGE,"E5.2.0.11"),sQuery(id+"F0.wireOp",EDGE,"E5.3.0.3"),sQuery(id+"F0.wireOp",EDGE,"E5.3.0.4"),sQuery(id+"F0.wireOp",EDGE,"E5.3.0.5"),sQuery(id+"F0.wireOp",EDGE,"E5.3.0.6"),sQuery(id+"F0.wireOp",EDGE,"E5.3.0.8"),sQuery(id+"F0.wireOp",EDGE,"E5.3.0.9"),sQuery(id+"F0.wireOp",EDGE,"E5.3.0.10"),sQuery(id+"F0.wireOp",EDGE,"E5.3.0.11"),sQuery(id+"F0.wireOp",EDGE,"E5.4.0.3"),sQuery(id+"F0.wireOp",EDGE,"E5.4.0.4"),sQuery(id+"F0.wireOp",EDGE,"E5.4.0.5"),sQuery(id+"F0.wireOp",EDGE,"E5.4.0.6"),sQuery(id+"F0.wireOp",EDGE,"E5.4.0.8"),sQuery(id+"F0.wireOp",EDGE,"E5.4.0.9"),sQuery(id+"F0.wireOp",EDGE,"E5.4.0.10"),sQuery(id+"F0.wireOp",EDGE,"E5.4.0.11"),sQuery(id+"F0.wireOp",EDGE,"E5.5.0.3"),sQuery(id+"F0.wireOp",EDGE,"E5.5.0.4"),sQuery(id+"F0.wireOp",EDGE,"E5.5.0.5"),sQuery(id+"F0.wireOp",EDGE,"E5.5.0.6"),sQuery(id+"F0.wireOp",EDGE,"E5.5.0.8"),sQuery(id+"F0.wireOp",EDGE,"E5.5.0.9"),sQuery(id+"F0.wireOp",EDGE,"E5.5.0.10"),sQuery(id+"F0.wireOp",EDGE,"E5.5.0.11"),sQuery(id+"F0.wireOp",EDGE,"E6.bottom"),sQuery(id+"F0.wireOp",EDGE,"E6.top"),sQuery(id+"F0.wireOp",EDGE,"E6.left"),sQuery(id+"F0.wireOp",EDGE,"E6.right"),sQuery(id+"F0.wireOp",EDGE,"E7.filletArc"),sQuery(id+"F0.wireOp",EDGE,"E8.filletArc"),sQuery(id+"F0.wireOp",EDGE,"E9.filletArc"),sQuery(id+"F0.wireOp",EDGE,"E10.filletArc"),sQuery(id+"F0.wireOp",EDGE,"E11.bottom"),sQuery(id+"F0.wireOp",EDGE,"E11.top"),sQuery(id+"F0.wireOp",EDGE,"E11.left"),sQuery(id+"F0.wireOp",EDGE,"E11.right"),sQuery(id+"F0.wireOp",EDGE,"E12.filletArc"),sQuery(id+"F0.wireOp",EDGE,"E13.filletArc"),sQuery(id+"F0.wireOp",EDGE,"E14.filletArc"),sQuery(id+"F0.wireOp",EDGE,"E15.filletArc"),sQuery(id+"F0.wireOp",EDGE,"E16.0.1.0"),sQuery(id+"F0.wireOp",EDGE,"E16.0.1.2"),sQuery(id+"F0.wireOp",EDGE,"E16.0.1.3"),sQuery(id+"F0.wireOp",EDGE,"E16.0.1.6"),sQuery(id+"F0.wireOp",EDGE,"E16.0.1.8"),sQuery(id+"F0.wireOp",EDGE,"E16.0.1.9"),sQuery(id+"F0.wireOp",EDGE,"E16.0.1.10"),sQuery(id+"F0.wireOp",EDGE,"E16.0.1.11"),sQuery(id+"F0.wireOp",EDGE,"E16.1.0.0"),sQuery(id+"F0.wireOp",EDGE,"E16.1.0.2"),sQuery(id+"F0.wireOp",EDGE,"E16.1.0.3"),sQuery(id+"F0.wireOp",EDGE,"E16.1.0.6"),sQuery(id+"F0.wireOp",EDGE,"E16.1.0.8"),sQuery(id+"F0.wireOp",EDGE,"E16.1.0.9"),sQuery(id+"F0.wireOp",EDGE,"E16.1.0.10"),sQuery(id+"F0.wireOp",EDGE,"E16.1.0.11"),sQuery(id+"F0.wireOp",EDGE,"E16.1.1.0"),sQuery(id+"F0.wireOp",EDGE,"E16.1.1.2"),sQuery(id+"F0.wireOp",EDGE,"E16.1.1.3"),sQuery(id+"F0.wireOp",EDGE,"E16.1.1.6"),sQuery(id+"F0.wireOp",EDGE,"E16.1.1.8"),sQuery(id+"F0.wireOp",EDGE,"E16.1.1.9"),sQuery(id+"F0.wireOp",EDGE,"E16.1.1.10"),sQuery(id+"F0.wireOp",EDGE,"E16.1.1.11"),sQuery(id+"F0.wireOp",EDGE,"E17.1.0.1"),sQuery(id+"F0.wireOp",EDGE,"E17.1.0.2"),sQuery(id+"F0.wireOp",EDGE,"E17.1.0.4"),sQuery(id+"F0.wireOp",EDGE,"E17.1.0.7"),sQuery(id+"F0.wireOp",EDGE,"E17.1.0.8"),sQuery(id+"F0.wireOp",EDGE,"E17.1.0.9"),sQuery(id+"F0.wireOp",EDGE,"E17.1.0.10"),sQuery(id+"F0.wireOp",EDGE,"E17.1.0.11"),sQuery(id+"F0.wireOp",EDGE,"E17.2.0.1"),sQuery(id+"F0.wireOp",EDGE,"E17.2.0.2"),sQuery(id+"F0.wireOp",EDGE,"E17.2.0.4"),sQuery(id+"F0.wireOp",EDGE,"E17.2.0.7"),sQuery(id+"F0.wireOp",EDGE,"E17.2.0.8"),sQuery(id+"F0.wireOp",EDGE,"E17.2.0.9"),sQuery(id+"F0.wireOp",EDGE,"E17.2.0.10"),sQuery(id+"F0.wireOp",EDGE,"E17.2.0.11"),sQuery(id+"F0.wireOp",EDGE,"E17.3.0.1"),sQuery(id+"F0.wireOp",EDGE,"E17.3.0.2"),sQuery(id+"F0.wireOp",EDGE,"E17.3.0.4"),sQuery(id+"F0.wireOp",EDGE,"E17.3.0.7"),sQuery(id+"F0.wireOp",EDGE,"E17.3.0.8"),sQuery(id+"F0.wireOp",EDGE,"E17.3.0.9"),sQuery(id+"F0.wireOp",EDGE,"E17.3.0.10"),sQuery(id+"F0.wireOp",EDGE,"E17.3.0.11"),sQuery(id+"F0.wireOp",EDGE,"E17.4.0.1"),sQuery(id+"F0.wireOp",EDGE,"E17.4.0.2"),sQuery(id+"F0.wireOp",EDGE,"E17.4.0.4"),sQuery(id+"F0.wireOp",EDGE,"E17.4.0.7"),sQuery(id+"F0.wireOp",EDGE,"E17.4.0.8"),sQuery(id+"F0.wireOp",EDGE,"E17.4.0.9"),sQuery(id+"F0.wireOp",EDGE,"E17.4.0.10"),sQuery(id+"F0.wireOp",EDGE,"E17.4.0.11"),sQuery(id+"F0.wireOp",EDGE,"E17.5.0.1"),sQuery(id+"F0.wireOp",EDGE,"E17.5.0.2"),sQuery(id+"F0.wireOp",EDGE,"E17.5.0.4"),sQuery(id+"F0.wireOp",EDGE,"E17.5.0.7"),sQuery(id+"F0.wireOp",EDGE,"E17.5.0.8"),sQuery(id+"F0.wireOp",EDGE,"E17.5.0.9"),sQuery(id+"F0.wireOp",EDGE,"E17.5.0.10"),sQuery(id+"F0.wireOp",EDGE,"E17.5.0.11"),sQuery(id+"F0.wireOp",EDGE,"E18.bottom"),sQuery(id+"F0.wireOp",EDGE,"E18.top"),sQuery(id+"F0.wireOp",EDGE,"E18.left"),sQuery(id+"F0.wireOp",EDGE,"E18.right"),sQuery(id+"F0.wireOp",EDGE,"E19.filletArc"),sQuery(id+"F0.wireOp",EDGE,"E20.filletArc"),sQuery(id+"F0.wireOp",EDGE,"E21.filletArc"),sQuery(id+"F0.wireOp",EDGE,"E22.filletArc"),sQuery(id+"F0.wireOp",EDGE,"E23.0.0.2"),sQuery(id+"F0.wireOp",EDGE,"E23.4.0.2"),sQuery(id+"F0.wireOp",EDGE,"E23.8.0.2"),sQuery(id+"F0.wireOp",EDGE,"E23.13.0.2"),sQuery(id+"F0.wireOp",EDGE,"E23.17.0.2"),sQuery(id+"F0.wireOp",EDGE,"E23.20.0.2"),sQuery(id+"F0.wireOp",EDGE,"E23.24.0.2"),sQuery(id+"F0.wireOp",EDGE,"E23.28.0.2"),sQuery(id+"F0.wireOp",EDGE,"E23.0.1.2"),sQuery(id+"F0.wireOp",EDGE,"E23.4.1.2"),sQuery(id+"F0.wireOp",EDGE,"E23.8.1.2"),sQuery(id+"F0.wireOp",EDGE,"E23.13.1.2"),sQuery(id+"F0.wireOp",EDGE,"E23.17.1.2"),sQuery(id+"F0.wireOp",EDGE,"E23.20.1.2"),sQuery(id+"F0.wireOp",EDGE,"E23.24.1.2"),sQuery(id+"F0.wireOp",EDGE,"E23.28.1.2"),sQuery(id+"F0.wireOp",EDGE,"E24.0.1.0"),sQuery(id+"F0.wireOp",EDGE,"E24.0.1.1"),sQuery(id+"F0.wireOp",EDGE,"E24.0.1.3"),sQuery(id+"F0.wireOp",EDGE,"E24.0.1.5"),sQuery(id+"F0.wireOp",EDGE,"E24.0.1.6"),sQuery(id+"F0.wireOp",EDGE,"E24.0.1.7"),sQuery(id+"F0.wireOp",EDGE,"E24.0.1.10"),sQuery(id+"F0.wireOp",EDGE,"E24.0.1.11"),sQuery(id+"F0.wireOp",EDGE,"E24.1.0.0"),sQuery(id+"F0.wireOp",EDGE,"E24.1.0.1"),sQuery(id+"F0.wireOp",EDGE,"E24.1.0.3"),sQuery(id+"F0.wireOp",EDGE,"E24.1.0.5"),sQuery(id+"F0.wireOp",EDGE,"E24.1.0.6"),sQuery(id+"F0.wireOp",EDGE,"E24.1.0.7"),sQuery(id+"F0.wireOp",EDGE,"E24.1.0.10"),sQuery(id+"F0.wireOp",EDGE,"E24.1.0.11"),sQuery(id+"F0.wireOp",EDGE,"E24.1.1.0"),sQuery(id+"F0.wireOp",EDGE,"E24.1.1.1"),sQuery(id+"F0.wireOp",EDGE,"E24.1.1.3"),sQuery(id+"F0.wireOp",EDGE,"E24.1.1.5"),sQuery(id+"F0.wireOp",EDGE,"E24.1.1.6"),sQuery(id+"F0.wireOp",EDGE,"E24.1.1.7"),sQuery(id+"F0.wireOp",EDGE,"E24.1.1.10"),sQuery(id+"F0.wireOp",EDGE,"E24.1.1.11"),sQuery(id+"F0.wireOp",EDGE,"E24.2.0.0"),sQuery(id+"F0.wireOp",EDGE,"E24.2.0.1"),sQuery(id+"F0.wireOp",EDGE,"E24.2.0.3"),sQuery(id+"F0.wireOp",EDGE,"E24.2.0.5"),sQuery(id+"F0.wireOp",EDGE,"E24.2.0.6"),sQuery(id+"F0.wireOp",EDGE,"E24.2.0.7"),sQuery(id+"F0.wireOp",EDGE,"E24.2.0.10"),sQuery(id+"F0.wireOp",EDGE,"E24.2.0.11"),sQuery(id+"F0.wireOp",EDGE,"E24.2.1.0"),sQuery(id+"F0.wireOp",EDGE,"E24.2.1.1"),sQuery(id+"F0.wireOp",EDGE,"E24.2.1.3"),sQuery(id+"F0.wireOp",EDGE,"E24.2.1.5"),sQuery(id+"F0.wireOp",EDGE,"E24.2.1.6"),sQuery(id+"F0.wireOp",EDGE,"E24.2.1.7"),sQuery(id+"F0.wireOp",EDGE,"E24.2.1.10"),sQuery(id+"F0.wireOp",EDGE,"E24.2.1.11"),sQuery(id+"F0.wireOp",EDGE,"E25"),sQuery(id+"F0.wireOp",EDGE,"E26"),sQuery(id+"F0.wireOp",EDGE,"E27"),sQuery(id+"F0.wireOp",EDGE,"E28"),sQuery(id+"F0.wireOp",EDGE,"E29"),sQuery(id+"F0.wireOp",EDGE,"E30"),sQuery(id+"F0.wireOp",EDGE,"E31.filletArc"),sQuery(id+"F0.wireOp",EDGE,"E32.filletArc"),sQuery(id+"F0.wireOp",EDGE,"E33.filletArc"),sQuery(id+"F0.wireOp",EDGE,"E34.filletArc"),sQuery(id+"F0.wireOp",EDGE,"E35.filletArc"),sQuery(id+"F0.wireOp",EDGE,"E36.filletArc"),sQuery(id+"F0.wireOp",EDGE,"E37.bottom"),sQuery(id+"F0.wireOp",EDGE,"E37.top"),sQuery(id+"F0.wireOp",EDGE,"E37.left"),sQuery(id+"F0.wireOp",EDGE,"E37.right"),sQuery(id+"F0.wireOp",EDGE,"E38.filletArc"),sQuery(id+"F0.wireOp",EDGE,"E39.filletArc"),sQuery(id+"F0.wireOp",EDGE,"E40.filletArc"),sQuery(id+"F0.wireOp",EDGE,"E41.filletArc")])],"isStart":true});
            var sketch = newSketch(context, id + "F2", { "sketchPlane" : qUnion([Q0])});
            skArc(sketch, "E42.0", {"start": v(-2.54, 0.95) * mm, "mid": v(-2.08, 2.08) * mm, "end": v(-0.95, 2.54) * mm});
            skLineSegment(sketch, "E42.1", {"start": v(-2.54, -67.5) * mm, "end": v(-2.54, 0.95) * mm});
            skArc(sketch, "E42.2", {"start": v(-0.95, -69.09) * mm, "mid": v(-2.08, -68.62) * mm, "end": v(-2.54, -67.5) * mm});
            skLineSegment(sketch, "E42.3", {"start": v(-0.95, -69.09) * mm, "end": v(140.14, -69.09) * mm});
            skArc(sketch, "E42.4", {"start": v(141.73, -67.5) * mm, "mid": v(141.27, -68.62) * mm, "end": v(140.14, -69.09) * mm});
            skLineSegment(sketch, "E42.5", {"start": v(-0.95, 2.54) * mm, "end": v(140.14, 2.54) * mm});
            skLineSegment(sketch, "E42.6", {"start": v(141.73, -67.5) * mm, "end": v(141.73, 0.95) * mm});
            skArc(sketch, "E42.7", {"start": v(140.14, 2.54) * mm, "mid": v(141.27, 2.08) * mm, "end": v(141.73, 0.95) * mm});
            skSolve(sketch);
        }
        {
            var Q0;
            Q0 = qSketchRegion(id + "F2", true);
            extrude(context, id + "F3", {"entities" : qUnion([Q0]), "operationType" : NewBodyOperationType.ADD, "depth" : 3.17 * mm});
        }
        {
            var Q0;
            Q0=makeQuery(id+"F3.boolean.opBoolean","MERGE",FACE,{"derivedFrom":[makeQuery(id+"F1.opExtrude","SWEPT_FACE",FACE,{"disambiguationData":[OSD([sQuery(id+"F0.wireOp",EDGE,"E37.top")])]}),makeQuery(id+"F3.opExtrude","SWEPT_FACE",FACE,{"disambiguationData":[OSD([sQuery(id+"F2.wireOp",EDGE,"E42.5")])]})]});
            var sketch = newSketch(context, id + "F4", { "sketchPlane" : qUnion([Q0])});
            skLineSegment(sketch, "E43", {"start": v(22.42, 26.14) * mm, "end": v(16.43, 15.66) * mm});
            skLineSegment(sketch, "E44", {"start": v(16.43, 15.66) * mm, "end": v(19.75, 15.66) * mm});
            skLineSegment(sketch, "E45", {"start": v(19.75, 15.66) * mm, "end": v(14.72, 8.6) * mm});
            skLineSegment(sketch, "E46", {"start": v(14.72, 8.6) * mm, "end": v(17.4, 8.6) * mm});
            skLineSegment(sketch, "E47", {"start": v(17.4, 8.6) * mm, "end": v(11.4, -1.45) * mm});
            skLineSegment(sketch, "E48", {"start": v(11.4, -1.45) * mm, "end": v(22, 10.2) * mm});
            skLineSegment(sketch, "E49", {"start": v(22, 10.2) * mm, "end": v(19, 10.2) * mm});
            skLineSegment(sketch, "E50", {"start": v(19, 10.2) * mm, "end": v(24.02, 17.48) * mm});
            skLineSegment(sketch, "E51", {"start": v(24.02, 17.48) * mm, "end": v(20.5, 17.48) * mm});
            skLineSegment(sketch, "E52", {"start": v(20.5, 17.48) * mm, "end": v(27.77, 26.14) * mm});
            skLineSegment(sketch, "E53", {"start": v(27.77, 26.14) * mm, "end": v(22.42, 26.14) * mm});
            skLineSegment(sketch, "E54", {"start": v(69.6, 28.58) * mm, "end": v(69.6, -3.17) * mm, "construction": true});
            skLineSegment(sketch, "E55.0.MirrorCS", {"start": v(124.47, 8.6) * mm, "end": v(121.8, 8.6) * mm});
            skLineSegment(sketch, "E55.1.MirrorCS", {"start": v(122.76, 15.66) * mm, "end": v(119.45, 15.66) * mm});
            skLineSegment(sketch, "E55.2.MirrorCS", {"start": v(117.2, 10.2) * mm, "end": v(120.2, 10.2) * mm});
            skLineSegment(sketch, "E55.3.MirrorCS", {"start": v(116.77, 26.14) * mm, "end": v(122.76, 15.66) * mm});
            skLineSegment(sketch, "E55.4.MirrorCS", {"start": v(118.7, 17.48) * mm, "end": v(111.43, 26.14) * mm});
            skLineSegment(sketch, "E55.5.MirrorCS", {"start": v(111.43, 26.14) * mm, "end": v(116.77, 26.14) * mm});
            skLineSegment(sketch, "E55.6.MirrorCS", {"start": v(121.8, 8.6) * mm, "end": v(127.79, -1.45) * mm});
            skLineSegment(sketch, "E55.7.MirrorCS", {"start": v(120.2, 10.2) * mm, "end": v(115.17, 17.48) * mm});
            skLineSegment(sketch, "E55.8.MirrorCS", {"start": v(115.17, 17.48) * mm, "end": v(118.7, 17.48) * mm});
            skLineSegment(sketch, "E55.9.MirrorCS", {"start": v(127.79, -1.45) * mm, "end": v(117.2, 10.2) * mm});
            skLineSegment(sketch, "E55.10.MirrorCS", {"start": v(119.45, 15.66) * mm, "end": v(124.47, 8.6) * mm});
            skSolve(sketch);
        }
        {
            var Q0;
            Q0 = qSketchRegion(id + "F4", true);
            extrude(context, id + "F5", {"entities" : qUnion([Q0]), "operationType" : NewBodyOperationType.REMOVE, "oppositeDirection" : true, "depth" : 0.76 * mm});
        }
        {
            var Q0;
            Q0=makeQuery(id+"F3.boolean.opBoolean","MERGE",FACE,{"derivedFrom":[makeQuery(id+"F1.opExtrude","SWEPT_FACE",FACE,{"disambiguationData":[OSD([sQuery(id+"F0.wireOp",EDGE,"E37.top")])]}),makeQuery(id+"F3.opExtrude","SWEPT_FACE",FACE,{"disambiguationData":[OSD([sQuery(id+"F2.wireOp",EDGE,"E42.5")])]})]});
            var sketch = newSketch(context, id + "F6", { "sketchPlane" : qUnion([Q0])});
            skLineSegment(sketch, "E56", {"start": v(38.53, 25.7) * mm, "end": v(33.59, 13.2) * mm});
            skLineSegment(sketch, "E57", {"start": v(33.59, 13.2) * mm, "end": v(37.63, 14.1) * mm});
            skLineSegment(sketch, "E58", {"start": v(37.63, 14.1) * mm, "end": v(29.74, -1.4) * mm});
            skLineSegment(sketch, "E59", {"start": v(29.74, -1.4) * mm, "end": v(42.58, 17.33) * mm});
            skLineSegment(sketch, "E60", {"start": v(42.58, 17.33) * mm, "end": v(38.02, 16) * mm});
            skLineSegment(sketch, "E61", {"start": v(38.02, 16) * mm, "end": v(43.36, 23.6) * mm});
            skLineSegment(sketch, "E62", {"start": v(43.36, 23.6) * mm, "end": v(46.43, 0) * mm});
            skLineSegment(sketch, "E63", {"start": v(48.13, 3.8) * mm, "end": v(46.91, 26.84) * mm});
            skLineSegment(sketch, "E64", {"start": v(46.91, 26.84) * mm, "end": v(38.53, 25.7) * mm});
            skLineSegment(sketch, "E65", {"start": v(48.13, 3.8) * mm, "end": v(53.7, 25.91) * mm});
            skLineSegment(sketch, "E66", {"start": v(53.7, 25.91) * mm, "end": v(54.26, 12.21) * mm});
            skLineSegment(sketch, "E67", {"start": v(54.26, 12.21) * mm, "end": v(52.84, 13.28) * mm});
            skLineSegment(sketch, "E68", {"start": v(52.84, 13.28) * mm, "end": v(48.4, -1.34) * mm});
            skLineSegment(sketch, "E69", {"start": v(48.4, -1.34) * mm, "end": v(46.43, 0) * mm});
            skLineSegment(sketch, "E70", {"start": v(64.12, 24.94) * mm, "end": v(57.5, 9.85) * mm});
            skLineSegment(sketch, "E71", {"start": v(57.5, 9.85) * mm, "end": v(60.05, 0) * mm});
            skLineSegment(sketch, "E72", {"start": v(60.05, 0) * mm, "end": v(68.6, 10.84) * mm});
            skLineSegment(sketch, "E73", {"start": v(68.6, 10.84) * mm, "end": v(64.12, 24.94) * mm});
            skLineSegment(sketch, "E74", {"start": v(63.27, 15.6) * mm, "end": v(61.46, 10.84) * mm});
            skLineSegment(sketch, "E75", {"start": v(61.46, 10.84) * mm, "end": v(61.46, 6.27) * mm});
            skLineSegment(sketch, "E76", {"start": v(61.46, 6.27) * mm, "end": v(65.08, 10.27) * mm});
            skLineSegment(sketch, "E77", {"start": v(65.08, 10.27) * mm, "end": v(63.27, 15.6) * mm});
            skLineSegment(sketch, "E78", {"start": v(81.75, 24.85) * mm, "end": v(79.18, 24.85) * mm});
            skLineSegment(sketch, "E79", {"start": v(79.18, 24.85) * mm, "end": v(74.5, 9.32) * mm});
            skLineSegment(sketch, "E80", {"start": v(74.5, 9.32) * mm, "end": v(77.08, 8.37) * mm});
            skLineSegment(sketch, "E81", {"start": v(77.08, 8.37) * mm, "end": v(73.04, 0) * mm});
            skLineSegment(sketch, "E82", {"start": v(73.04, 0) * mm, "end": v(81.74, 9.07) * mm});
            skLineSegment(sketch, "E83", {"start": v(81.74, 9.07) * mm, "end": v(88.81, 0) * mm});
            skLineSegment(sketch, "E84", {"start": v(88.81, 0) * mm, "end": v(85.75, 18.46) * mm});
            skLineSegment(sketch, "E85", {"start": v(85.75, 18.46) * mm, "end": v(83.65, 19.23) * mm});
            skLineSegment(sketch, "E86", {"start": v(83.65, 19.23) * mm, "end": v(81.75, 24.85) * mm});
            skLineSegment(sketch, "E87", {"start": v(78, 13.44) * mm, "end": v(84.76, 13.42) * mm});
            skLineSegment(sketch, "E88", {"start": v(84.76, 13.42) * mm, "end": v(84.76, 11.42) * mm});
            skLineSegment(sketch, "E89", {"start": v(84.76, 11.42) * mm, "end": v(78, 13.44) * mm});
            skLineSegment(sketch, "E90", {"start": v(99.57, 25.05) * mm, "end": v(103.39, 12.18) * mm});
            skLineSegment(sketch, "E91", {"start": v(105.18, 12.18) * mm, "end": v(103.39, 12.18) * mm});
            skLineSegment(sketch, "E92", {"start": v(105.18, 12.18) * mm, "end": v(107.84, 0) * mm});
            skLineSegment(sketch, "E93", {"start": v(107.84, 0) * mm, "end": v(104.84, 0) * mm});
            skLineSegment(sketch, "E94", {"start": v(104.84, 0) * mm, "end": v(100.23, 10.75) * mm});
            skLineSegment(sketch, "E95", {"start": v(100.23, 10.75) * mm, "end": v(93.95, 10.75) * mm});
            skLineSegment(sketch, "E96", {"start": v(93.95, 10.75) * mm, "end": v(95.68, 0) * mm});
            skLineSegment(sketch, "E97", {"start": v(95.68, 0) * mm, "end": v(92.79, -0.46) * mm});
            skLineSegment(sketch, "E98", {"start": v(92.79, -0.46) * mm, "end": v(92.68, 14.16) * mm});
            skLineSegment(sketch, "E99", {"start": v(90.21, 14.16) * mm, "end": v(92.68, 14.16) * mm});
            skLineSegment(sketch, "E100", {"start": v(90.21, 14.16) * mm, "end": v(89.2, 25.26) * mm});
            skLineSegment(sketch, "E101", {"start": v(89.2, 25.26) * mm, "end": v(91.84, 25.26) * mm});
            skLineSegment(sketch, "E102", {"start": v(91.84, 25.26) * mm, "end": v(95.44, 14.52) * mm});
            skLineSegment(sketch, "E103", {"start": v(95.44, 14.52) * mm, "end": v(99.82, 14.52) * mm});
            skLineSegment(sketch, "E104", {"start": v(99.82, 14.52) * mm, "end": v(97.08, 25.7) * mm});
            skLineSegment(sketch, "E105", {"start": v(97.08, 25.7) * mm, "end": v(99.57, 25.05) * mm});
            skSolve(sketch);
        }
        {
            var Q0;
            Q0 = qSketchRegion(id + "F6", true);
            extrude(context, id + "F7", {"entities" : qUnion([Q0]), "operationType" : NewBodyOperationType.ADD, "depth" : 0.76 * mm});
        }
    });
